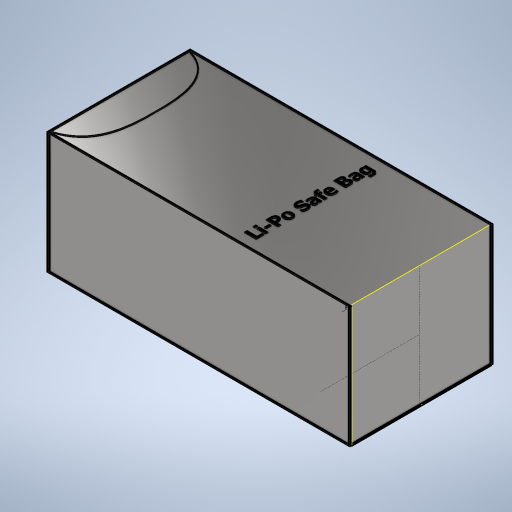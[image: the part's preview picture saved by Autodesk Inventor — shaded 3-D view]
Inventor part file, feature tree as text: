
AUTODESK INVENTOR PART (.ipt)
format: ipt  version: 2023 (Build 270158000, 158)  size: 696,320 bytes
history: native  units: mm
features: sketch x6, extrude x5, projected_geometry x1
ambient origin geometry x8: Origin, YZ Plane, XZ Plane, XY Plane, X Axis, Y Axis, Z Axis, Center Point
bodies: Solide1 (feature_tree)
feature tree (12):
  extrude  "Extrusion1"  Depth=150.0mm
  sketch  "Esquisse2"
  extrude  "Extrusion5"  Depth=70.0mm
  extrude  "Extrusion7"  Depth=60.0mm TaperAngle=0.0deg
  sketch  "Esquisse9"
  extrude  "Extrusion8"  Depth=0.5mm
  extrude  "Extrusion9"  Depth=0.5mm
  sketch  "Esquisse10"
  sketch  "Esquisse1"
  sketch  "Esquisse6"
  sketch  "Esquisse8"
  projected_geometry  "Boucle projetée2"
